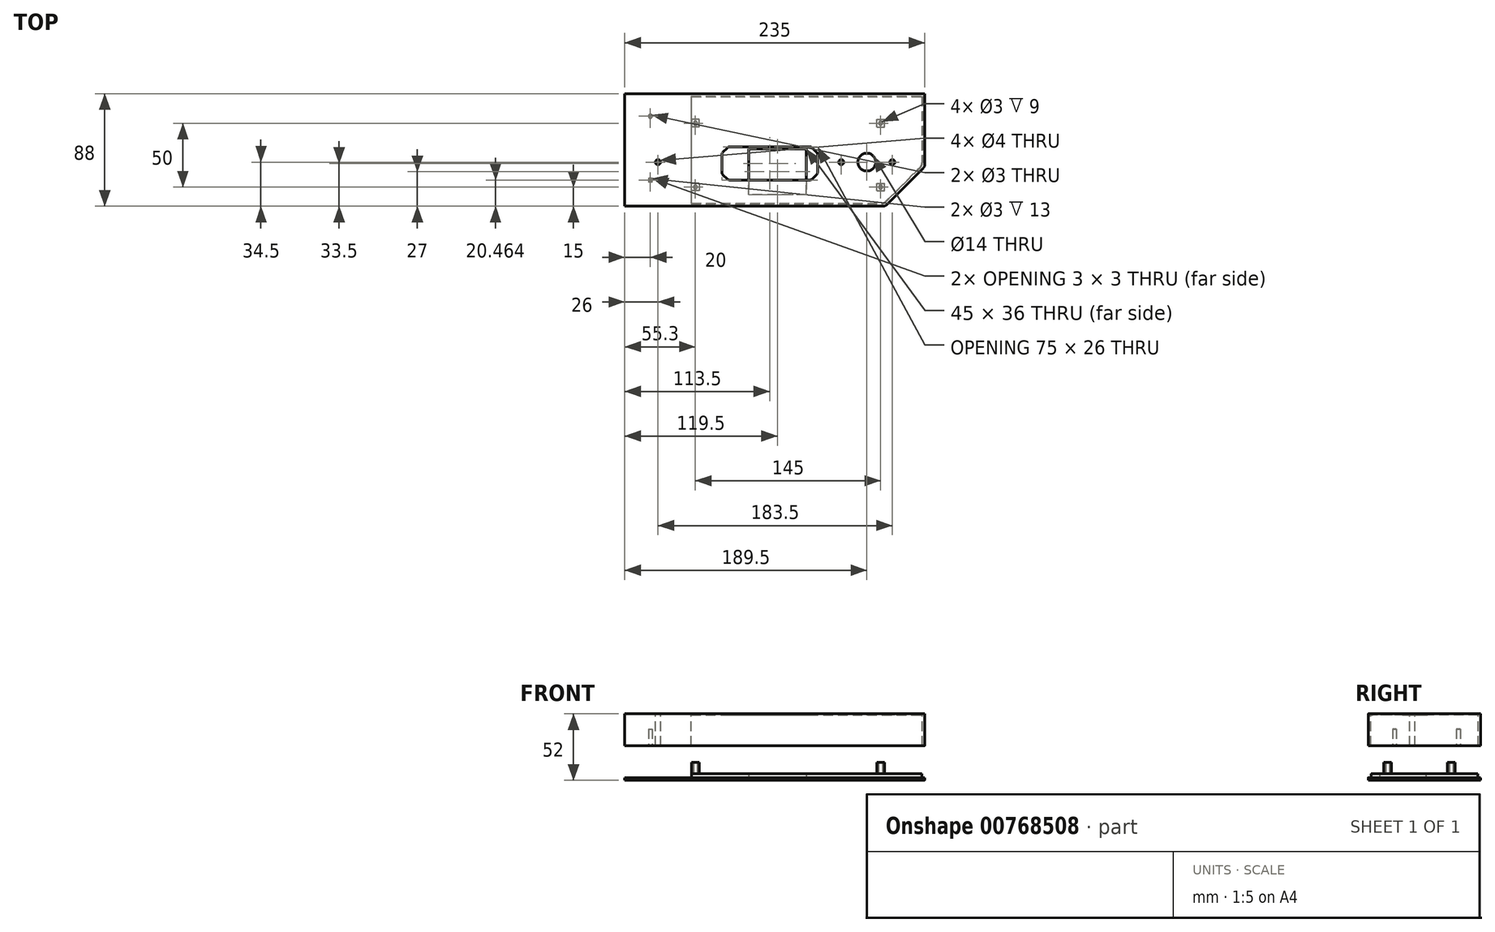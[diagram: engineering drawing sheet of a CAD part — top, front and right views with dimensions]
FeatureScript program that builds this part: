
annotation { "Feature Type Name" : "Feature", "Feature Type Description" : "" }
export const myFeature = defineFeature(function(context is Context, id is Id, definition is map)
    precondition{}
    {
        {
            var Q0;
            Q0=qCreatedBy(makeId("Top.planeOp"),FACE);
            var sketch = newSketch(context, id + "F0", { "sketchPlane" : qUnion([Q0])});
            skLineSegment(sketch, "E0.bottom", {"start": v(0, 0) * mm, "end": v(154, 0) * mm});
            skLineSegment(sketch, "E0.top", {"start": v(2, 68) * mm, "end": v(154, 68) * mm});
            skLineSegment(sketch, "E0.left", {"start": v(0, 0) * mm, "end": v(0, 68) * mm});
            skLineSegment(sketch, "E0.right", {"start": v(154, 2.83) * mm, "end": v(154, 68) * mm});
            skLineSegment(sketch, "E1", {"start": v(154, 0) * mm, "end": v(185, 31) * mm});
            skLineSegment(sketch, "E2.bottom", {"start": v(2, 68) * mm, "end": v(183, 68) * mm});
            skLineSegment(sketch, "E2.top", {"start": v(0, 88) * mm, "end": v(185, 88) * mm});
            skLineSegment(sketch, "E2.left", {"start": v(0, 68) * mm, "end": v(0, 88) * mm});
            skLineSegment(sketch, "E3.bottom", {"start": v(26, 20.5) * mm, "end": v(101, 20.5) * mm});
            skLineSegment(sketch, "E3.top", {"start": v(26, 46.5) * mm, "end": v(101, 46.5) * mm});
            skLineSegment(sketch, "E3.left", {"start": v(26, 20.5) * mm, "end": v(26, 46.5) * mm});
            skLineSegment(sketch, "E3.right", {"start": v(101, 20.5) * mm, "end": v(101, 46.5) * mm});
            skCircle(sketch, "E4", {"center": v(139.5, 34.5) * mm, "radius": 7 * mm});
            skLineSegment(sketch, "E5", {"start": v(2, 86) * mm, "end": v(2, 2) * mm});
            skLineSegment(sketch, "E6", {"start": v(2, 2) * mm, "end": v(153.17, 2) * mm});
            skLineSegment(sketch, "E7.trimOffspring", {"start": v(2, 86) * mm, "end": v(183, 86) * mm});
            skLineSegment(sketch, "E8", {"start": v(185, 31) * mm, "end": v(185, 88) * mm});
            skLineSegment(sketch, "E9", {"start": v(183, 86) * mm, "end": v(183, 31.83) * mm});
            skLineSegment(sketch, "E10.trimOffspring", {"start": v(183, 31.83) * mm, "end": v(153.17, 2) * mm});
            skCircle(sketch, "E11", {"center": v(119.5, 34.5) * mm, "radius": 2 * mm});
            skCircle(sketch, "E12", {"center": v(159.5, 34.5) * mm, "radius": 2 * mm});
            skCircle(sketch, "E13", {"center": v(-20, 34.5) * mm, "radius": 2 * mm});
            skSolve(sketch);
        }
        {
            var Q0;
            {var subQ1=sQuery(id+"F0.wireOp",EDGE,"E0.right");Q0=makeQuery(id+"F0.imprint","IMPRINT",FACE,{"disambiguationData":[TD([[makeQuery(id+"F0.imprint","IMPRINT",EDGE,{"derivedFrom":subQ1}),1.0]])]});}
            var Q1;
            {var subQ0=sQuery(id+"F0.wireOp",EDGE,"E0.right");Q1=makeQuery(id+"F0.imprint","IMPRINT",FACE,{"disambiguationData":[TD([[makeQuery(id+"F0.imprint","IMPRINT",EDGE,{"derivedFrom":subQ0}),-1.0]])]});}
            var Q2;
            {var subQ3=sQuery(id+"F0.wireOp",EDGE,"E7.trimOffspring");Q2=makeQuery(id+"F0.imprint","IMPRINT",FACE,{"disambiguationData":[TD([[makeQuery(id+"F0.imprint","IMPRINT",EDGE,{"derivedFrom":subQ3}),-1.0]])]});}
            extrude(context, id + "F1", {"entities" : qUnion([Q0, Q1, Q2]), "oppositeDirection" : true, "depth" : 1 * mm, "offsetDistance" : 25 * mm});
        }
        {
            var Q0;
            Q0=makeQuery(id+"F0.imprint","IMPRINT",FACE,{"disambiguationData":[TD([[makeQuery(id+"F0.imprint","IMPRINT",EDGE,{"derivedFrom":sQuery(id+"F0.wireOp",EDGE,"E0.bottom")}),1.0]])]});
            extrude(context, id + "F2", {"entities" : qUnion([Q0]), "operationType" : NewBodyOperationType.ADD, "oppositeDirection" : true, "depth" : 25 * mm, "offsetDistance" : 25 * mm});
        }
        {
            var Q0;
            Q0=makeQuery(id+"F2.opExtrude","SWEPT_EDGE",EDGE,{"disambiguationData":[OSD([sQuery(id+"F0.wireOp",EDGE,"E0.bottom"),sQuery(id+"F0.wireOp",EDGE,"E1")])]});
            var Q1;
            Q1=makeQuery(id+"F2.opExtrude","SWEPT_EDGE",EDGE,{"disambiguationData":[OSD([sQuery(id+"F0.wireOp",EDGE,"E1"),sQuery(id+"F0.wireOp",EDGE,"E8")])]});
            var Q2;
            Q2=makeQuery(id+"F2.opExtrude","SWEPT_EDGE",EDGE,{"disambiguationData":[OSD([sQuery(id+"F0.wireOp",EDGE,"E6"),sQuery(id+"F0.wireOp",EDGE,"E10.trimOffspring")])]});
            var Q3;
            Q3=makeQuery(id+"F2.opExtrude","SWEPT_EDGE",EDGE,{"disambiguationData":[OSD([sQuery(id+"F0.wireOp",EDGE,"E9"),sQuery(id+"F0.wireOp",EDGE,"E10.trimOffspring")])]});
            fillet(context, id + "F3", {"entities" : qUnion([Q0, Q1, Q2, Q3]), "radius" : 5 * mm, "tangentPropagation" : true, "allowEdgeOverflow" : false});
        }
        {
            var Q0;
            Q0=makeQuery(id+"F1.opExtrude","SWEPT_EDGE",EDGE,{"disambiguationData":[OSD([sQuery(id+"F0.wireOp",EDGE,"E3.top"),sQuery(id+"F0.wireOp",EDGE,"E3.left")])]});
            var Q1;
            Q1=makeQuery(id+"F1.opExtrude","SWEPT_EDGE",EDGE,{"disambiguationData":[OSD([sQuery(id+"F0.wireOp",EDGE,"E3.bottom"),sQuery(id+"F0.wireOp",EDGE,"E3.left")])]});
            var Q2;
            Q2=makeQuery(id+"F1.opExtrude","SWEPT_EDGE",EDGE,{"disambiguationData":[OSD([sQuery(id+"F0.wireOp",EDGE,"E3.bottom"),sQuery(id+"F0.wireOp",EDGE,"E3.right")])]});
            var Q3;
            Q3=makeQuery(id+"F1.opExtrude","SWEPT_EDGE",EDGE,{"disambiguationData":[OSD([sQuery(id+"F0.wireOp",EDGE,"E3.top"),sQuery(id+"F0.wireOp",EDGE,"E3.right")])]});
            chamfer(context, id + "F4", {"entities" : qUnion([Q0, Q1, Q2, Q3]), "width" : 5 * mm, "tangentPropagation" : true});
        }
        {
            var Q0;
            {var subQ0=sQuery(id+"F0.wireOp",EDGE,"E3.left");Q0=makeQuery(id+"F4.opChamfer","BLEND_EDGE",EDGE,{"blendedFrom":[makeQuery(id+"F1.opExtrude","SWEPT_EDGE",EDGE,{"disambiguationData":[OSD([sQuery(id+"F0.wireOp",EDGE,"E3.top"),subQ0])]}),makeQuery(id+"F1.opExtrude","SWEPT_FACE",FACE,{"disambiguationData":[OSD([subQ0])]})],"blendedInto":[makeQuery(id+"F1.opExtrude","SWEPT_FACE",FACE,{"disambiguationData":[OSD([subQ0])]})]});}
            var Q1;
            {var subQ0=sQuery(id+"F0.wireOp",EDGE,"E3.top");Q1=makeQuery(id+"F4.opChamfer","BLEND_EDGE",EDGE,{"blendedFrom":[makeQuery(id+"F1.opExtrude","SWEPT_EDGE",EDGE,{"disambiguationData":[OSD([subQ0,sQuery(id+"F0.wireOp",EDGE,"E3.left")])]}),makeQuery(id+"F1.opExtrude","SWEPT_FACE",FACE,{"disambiguationData":[OSD([subQ0])]})],"blendedInto":[makeQuery(id+"F1.opExtrude","SWEPT_FACE",FACE,{"disambiguationData":[OSD([subQ0])]})]});}
            var Q2;
            {var subQ0=sQuery(id+"F0.wireOp",EDGE,"E3.left");Q2=makeQuery(id+"F4.opChamfer","BLEND_EDGE",EDGE,{"blendedFrom":[makeQuery(id+"F1.opExtrude","SWEPT_EDGE",EDGE,{"disambiguationData":[OSD([sQuery(id+"F0.wireOp",EDGE,"E3.bottom"),subQ0])]}),makeQuery(id+"F1.opExtrude","SWEPT_FACE",FACE,{"disambiguationData":[OSD([subQ0])]})],"blendedInto":[makeQuery(id+"F1.opExtrude","SWEPT_FACE",FACE,{"disambiguationData":[OSD([subQ0])]})]});}
            var Q3;
            {var subQ0=sQuery(id+"F0.wireOp",EDGE,"E3.bottom");Q3=makeQuery(id+"F4.opChamfer","BLEND_EDGE",EDGE,{"blendedFrom":[makeQuery(id+"F1.opExtrude","SWEPT_EDGE",EDGE,{"disambiguationData":[OSD([subQ0,sQuery(id+"F0.wireOp",EDGE,"E3.left")])]}),makeQuery(id+"F1.opExtrude","SWEPT_FACE",FACE,{"disambiguationData":[OSD([subQ0])]})],"blendedInto":[makeQuery(id+"F1.opExtrude","SWEPT_FACE",FACE,{"disambiguationData":[OSD([subQ0])]})]});}
            var Q4;
            {var subQ0=sQuery(id+"F0.wireOp",EDGE,"E3.top");Q4=makeQuery(id+"F4.opChamfer","BLEND_EDGE",EDGE,{"blendedFrom":[makeQuery(id+"F1.opExtrude","SWEPT_EDGE",EDGE,{"disambiguationData":[OSD([subQ0,sQuery(id+"F0.wireOp",EDGE,"E3.right")])]}),makeQuery(id+"F1.opExtrude","SWEPT_FACE",FACE,{"disambiguationData":[OSD([subQ0])]})],"blendedInto":[makeQuery(id+"F1.opExtrude","SWEPT_FACE",FACE,{"disambiguationData":[OSD([subQ0])]})]});}
            var Q5;
            {var subQ0=sQuery(id+"F0.wireOp",EDGE,"E3.right");Q5=makeQuery(id+"F4.opChamfer","BLEND_EDGE",EDGE,{"blendedFrom":[makeQuery(id+"F1.opExtrude","SWEPT_EDGE",EDGE,{"disambiguationData":[OSD([sQuery(id+"F0.wireOp",EDGE,"E3.top"),subQ0])]}),makeQuery(id+"F1.opExtrude","SWEPT_FACE",FACE,{"disambiguationData":[OSD([subQ0])]})],"blendedInto":[makeQuery(id+"F1.opExtrude","SWEPT_FACE",FACE,{"disambiguationData":[OSD([subQ0])]})]});}
            var Q6;
            {var subQ0=sQuery(id+"F0.wireOp",EDGE,"E3.right");Q6=makeQuery(id+"F4.opChamfer","BLEND_EDGE",EDGE,{"blendedFrom":[makeQuery(id+"F1.opExtrude","SWEPT_EDGE",EDGE,{"disambiguationData":[OSD([sQuery(id+"F0.wireOp",EDGE,"E3.bottom"),subQ0])]}),makeQuery(id+"F1.opExtrude","SWEPT_FACE",FACE,{"disambiguationData":[OSD([subQ0])]})],"blendedInto":[makeQuery(id+"F1.opExtrude","SWEPT_FACE",FACE,{"disambiguationData":[OSD([subQ0])]})]});}
            var Q7;
            {var subQ0=sQuery(id+"F0.wireOp",EDGE,"E3.bottom");Q7=makeQuery(id+"F4.opChamfer","BLEND_EDGE",EDGE,{"blendedFrom":[makeQuery(id+"F1.opExtrude","SWEPT_EDGE",EDGE,{"disambiguationData":[OSD([subQ0,sQuery(id+"F0.wireOp",EDGE,"E3.right")])]}),makeQuery(id+"F1.opExtrude","SWEPT_FACE",FACE,{"disambiguationData":[OSD([subQ0])]})],"blendedInto":[makeQuery(id+"F1.opExtrude","SWEPT_FACE",FACE,{"disambiguationData":[OSD([subQ0])]})]});}
            fillet(context, id + "F5", {"entities" : qUnion([Q0, Q1, Q2, Q3, Q4, Q5, Q6, Q7]), "radius" : 3 * mm, "tangentPropagation" : true, "allowEdgeOverflow" : false});
        }
        {
            var Q0;
            Q0=qCreatedBy(makeId("Top.planeOp"),FACE);
            var sketch = newSketch(context, id + "F6", { "sketchPlane" : qUnion([Q0])});
            skLineSegment(sketch, "E14.bottom", {"start": v(0, 0) * mm, "end": v(-50, 0) * mm});
            skLineSegment(sketch, "E14.top", {"start": v(0, 88) * mm, "end": v(-50, 88) * mm});
            skLineSegment(sketch, "E14.left", {"start": v(0, 0) * mm, "end": v(0, 88) * mm});
            skLineSegment(sketch, "E14.right", {"start": v(-50, 0) * mm, "end": v(-50, 88) * mm});
            skSolve(sketch);
        }
        {
            var Q0;
            Q0=makeQuery(id+"F6.imprint","IMPRINT",FACE,{"disambiguationData":[TD([[makeQuery(id+"F6.imprint","IMPRINT",EDGE,{"derivedFrom":sQuery(id+"F6.wireOp",EDGE,"E14.bottom")}),-1.0]])]});
            extrude(context, id + "F7", {"entities" : qUnion([Q0]), "operationType" : NewBodyOperationType.ADD, "oppositeDirection" : true, "depth" : 25 * mm, "offsetDistance" : 25 * mm});
        }
        {
            var Q0;
            Q0=qCreatedBy(makeId("Top.planeOp"),FACE);
            cPlane(context, id + "F8", {"entities" : qUnion([Q0]), "cplaneType" : CPlaneType.OFFSET, "offset" : 50 * mm, "oppositeDirection" : true, "width" : 150 * mm, "height" : 150 * mm});
        }
        {
            var Q0;
            Q0=qCreatedBy(id+"F8.planeOp",FACE);
            var sketch = newSketch(context, id + "F9", { "sketchPlane" : qUnion([Q0])});
            skLineSegment(sketch, "E15.bottom", {"start": v(0, 0) * mm, "end": v(154, 0) * mm});
            skLineSegment(sketch, "E15.top", {"start": v(0, 88) * mm, "end": v(185, 88) * mm});
            skLineSegment(sketch, "E15.left", {"start": v(0, 0) * mm, "end": v(0, 88) * mm});
            skLineSegment(sketch, "E16", {"start": v(154, 0) * mm, "end": v(185, 31) * mm});
            skLineSegment(sketch, "E17", {"start": v(2.3, 2.3) * mm, "end": v(153.05, 2.3) * mm});
            skLineSegment(sketch, "E18", {"start": v(2.3, 85.7) * mm, "end": v(182.7, 85.7) * mm});
            skLineSegment(sketch, "E19", {"start": v(153.05, 2.3) * mm, "end": v(182.7, 31.95) * mm});
            skPoint(sketch, "E20.orphan", {"position": v(150.75, 0) * mm});
            skLineSegment(sketch, "E21.trimOffspring", {"start": v(2.3, 2.3) * mm, "end": v(2.3, 85.9) * mm});
            skLineSegment(sketch, "E22", {"start": v(185, 31) * mm, "end": v(185, 88) * mm});
            skLineSegment(sketch, "E23.trimOffspring", {"start": v(182.7, 85.7) * mm, "end": v(182.7, 31.95) * mm});
            skSolve(sketch);
        }
        {
            var Q0;
            {var subQ0=sQuery(id+"F9.wireOp",EDGE,"E17");Q0=makeQuery(id+"F9.imprint","IMPRINT",FACE,{"disambiguationData":[TD([[makeQuery(id+"F9.imprint","IMPRINT",EDGE,{"derivedFrom":subQ0}),1.0]])]});}
            extrude(context, id + "F10", {"entities" : qUnion([Q0]), "depth" : 3 * mm, "offsetDistance" : 25 * mm});
        }
        {
            var Q0;
            Q0 = qSketchRegion(id + "F9", true);
            var Q1;
            Q1=makeQuery(id+"F10.opExtrude","CAP_FACE",FACE,{"disambiguationData":[OSD([sQuery(id+"F9.wireOp",EDGE,"E17"),sQuery(id+"F9.wireOp",EDGE,"E18"),sQuery(id+"F9.wireOp",EDGE,"E19"),sQuery(id+"F9.wireOp",EDGE,"E21.trimOffspring")])],"isStart":true});
            extrude(context, id + "F11", {"entities" : qUnion([Q0, Q1]), "operationType" : NewBodyOperationType.ADD, "oppositeDirection" : true, "depth" : 2 * mm, "offsetDistance" : 25 * mm});
        }
        {
            var Q0;
            Q0=makeQuery(id+"F11.opExtrude","SWEPT_FACE",FACE,{"disambiguationData":[OSD([sQuery(id+"F9.wireOp",EDGE,"E15.left")])]});
            extrude(context, id + "F12", {"entities" : qUnion([Q0]), "operationType" : NewBodyOperationType.ADD, "depth" : 50 * mm, "offsetDistance" : 25 * mm});
        }
        {
            var Q0;
            Q0=makeQuery(id+"F10.opExtrude","SWEPT_EDGE",EDGE,{"disambiguationData":[OSD([sQuery(id+"F9.wireOp",EDGE,"E17"),sQuery(id+"F9.wireOp",EDGE,"E19")])]});
            var Q1;
            Q1=makeQuery(id+"F11.opExtrude","SWEPT_EDGE",EDGE,{"disambiguationData":[OSD([sQuery(id+"F9.wireOp",EDGE,"E15.bottom"),sQuery(id+"F9.wireOp",EDGE,"E16")])]});
            var Q2;
            Q2=makeQuery(id+"F10.opExtrude","SWEPT_EDGE",EDGE,{"disambiguationData":[OSD([sQuery(id+"F9.wireOp",EDGE,"E19"),sQuery(id+"F9.wireOp",EDGE,"E23.trimOffspring")])]});
            var Q3;
            Q3=makeQuery(id+"F11.opExtrude","SWEPT_EDGE",EDGE,{"disambiguationData":[OSD([sQuery(id+"F9.wireOp",EDGE,"E16"),sQuery(id+"F9.wireOp",EDGE,"E22")])]});
            fillet(context, id + "F13", {"entities" : qUnion([Q0, Q1, Q2, Q3]), "radius" : 5 * mm, "tangentPropagation" : true, "allowEdgeOverflow" : false});
        }
        {
            var Q0;
            {var subQ0=sQuery(id+"F9.wireOp",EDGE,"E15.left");var subQ1=sQuery(id+"F9.wireOp",EDGE,"E21.trimOffspring");var subQ2=sQuery(id+"F9.wireOp",EDGE,"E19");var subQ3=sQuery(id+"F9.wireOp",EDGE,"E18");var subQ4=sQuery(id+"F9.wireOp",EDGE,"E17");Q0=makeQuery(id+"F12.boolean.opBoolean","MERGE",FACE,{"derivedFrom":[makeQuery(id+"F11.boolean.opBoolean","MERGE",FACE,{"derivedFrom":[makeQuery(id+"F11.opExtrude","CAP_FACE",FACE,{"disambiguationData":[OSD([sQuery(id+"F9.wireOp",EDGE,"E15.bottom"),sQuery(id+"F9.wireOp",EDGE,"E15.top"),subQ0,sQuery(id+"F9.wireOp",EDGE,"E16"),subQ4,subQ3,subQ2,subQ1])],"isStart":false}),makeQuery(id+"F11.opExtrude","CAP_FACE",FACE,{"disambiguationData":[OSD([subQ4,subQ3,subQ2,subQ1])],"isStart":false})]}),makeQuery(id+"F12.opExtrude","SWEPT_FACE",FACE,{"disambiguationData":[OSD([subQ0]),TDD([makeQuery(id+"F11.opExtrude","CAP_EDGE",EDGE,{"disambiguationData":[OSD([subQ0])],"isStart":false})])]})]});}
            var sketch = newSketch(context, id + "F14", { "sketchPlane" : qUnion([Q0])});
            skLineSegment(sketch, "E24.bottom", {"start": v(47, -34) * mm, "end": v(92, -34) * mm});
            skLineSegment(sketch, "E24.top", {"start": v(47, -45) * mm, "end": v(92, -45) * mm});
            skLineSegment(sketch, "E24.left", {"start": v(47, -34) * mm, "end": v(47, -45) * mm});
            skLineSegment(sketch, "E24.right", {"start": v(92, -34) * mm, "end": v(92, -45) * mm});
            skCircle(sketch, "E25", {"center": v(5.3, -65) * mm, "radius": 1.5 * mm});
            skCircle(sketch, "E26", {"center": v(150.3, -65) * mm, "radius": 1.5 * mm});
            skCircle(sketch, "E27", {"center": v(150.3, -15) * mm, "radius": 1.5 * mm});
            skCircle(sketch, "E28", {"center": v(5.3, -15) * mm, "radius": 1.5 * mm});
            skLineSegment(sketch, "E29.bottom", {"start": v(2.3, -68) * mm, "end": v(8.3, -68) * mm});
            skLineSegment(sketch, "E29.top", {"start": v(2.3, -62) * mm, "end": v(8.3, -62) * mm});
            skLineSegment(sketch, "E29.left", {"start": v(2.3, -68) * mm, "end": v(2.3, -62) * mm});
            skLineSegment(sketch, "E29.right", {"start": v(8.3, -68) * mm, "end": v(8.3, -62) * mm});
            skLineSegment(sketch, "E30.bottom", {"start": v(153.3, -68) * mm, "end": v(147.3, -68) * mm});
            skLineSegment(sketch, "E30.top", {"start": v(153.3, -62) * mm, "end": v(147.3, -62) * mm});
            skLineSegment(sketch, "E30.left", {"start": v(153.3, -68) * mm, "end": v(153.3, -62) * mm});
            skLineSegment(sketch, "E30.right", {"start": v(147.3, -68) * mm, "end": v(147.3, -62) * mm});
            skLineSegment(sketch, "E31.bottom", {"start": v(2.3, -12) * mm, "end": v(8.3, -12) * mm});
            skLineSegment(sketch, "E31.top", {"start": v(2.3, -18) * mm, "end": v(8.3, -18) * mm});
            skLineSegment(sketch, "E31.left", {"start": v(2.3, -12) * mm, "end": v(2.3, -18) * mm});
            skLineSegment(sketch, "E31.right", {"start": v(8.3, -12) * mm, "end": v(8.3, -18) * mm});
            skLineSegment(sketch, "E32.bottom", {"start": v(153.3, -18) * mm, "end": v(147.3, -18) * mm});
            skLineSegment(sketch, "E32.top", {"start": v(153.3, -12) * mm, "end": v(147.3, -12) * mm});
            skLineSegment(sketch, "E32.left", {"start": v(153.3, -18) * mm, "end": v(153.3, -12) * mm});
            skLineSegment(sketch, "E32.right", {"start": v(147.3, -18) * mm, "end": v(147.3, -12) * mm});
            skSolve(sketch);
        }
        {
            var Q0;
            Q0=makeQuery(id+"F14.imprint","IMPRINT",FACE,{"disambiguationData":[TD([[makeQuery(id+"F14.imprint","IMPRINT",EDGE,{"derivedFrom":sQuery(id+"F14.wireOp",EDGE,"E24.bottom")}),-1.0]])]});
            extrude(context, id + "F15", {"entities" : qUnion([Q0]), "operationType" : NewBodyOperationType.REMOVE, "oppositeDirection" : true, "depth" : 25 * mm, "offsetDistance" : 25 * mm});
        }
        {
            var Q0;
            Q0=makeQuery(id+"F14.imprint","IMPRINT",FACE,{"disambiguationData":[TD([[makeQuery(id+"F14.imprint","IMPRINT",EDGE,{"derivedFrom":sQuery(id+"F14.wireOp",EDGE,"E25")}),-1.0]])]});
            var Q1;
            Q1=makeQuery(id+"F14.imprint","IMPRINT",FACE,{"disambiguationData":[TD([[makeQuery(id+"F14.imprint","IMPRINT",EDGE,{"derivedFrom":sQuery(id+"F14.wireOp",EDGE,"E26")}),-1.0]])]});
            var Q2;
            Q2=makeQuery(id+"F14.imprint","IMPRINT",FACE,{"disambiguationData":[TD([[makeQuery(id+"F14.imprint","IMPRINT",EDGE,{"derivedFrom":sQuery(id+"F14.wireOp",EDGE,"E27")}),-1.0]])]});
            var Q3;
            Q3=makeQuery(id+"F14.imprint","IMPRINT",FACE,{"disambiguationData":[TD([[makeQuery(id+"F14.imprint","IMPRINT",EDGE,{"derivedFrom":sQuery(id+"F14.wireOp",EDGE,"E28")}),-1.0]])]});
            extrude(context, id + "F16", {"entities" : qUnion([Q0, Q1, Q2, Q3]), "operationType" : NewBodyOperationType.ADD, "oppositeDirection" : true, "depth" : (9 + 5) * mm, "offsetDistance" : 25 * mm});
        }
        {
            var Q0;
            Q0=makeQuery(id+"F14.imprint","IMPRINT",FACE,{"disambiguationData":[TD([[makeQuery(id+"F14.imprint","IMPRINT",EDGE,{"derivedFrom":sQuery(id+"F14.wireOp",EDGE,"E24.bottom")}),1.0]])]});
            var sketch = newSketch(context, id + "F17", { "sketchPlane" : qUnion([Q0])});
            skCircle(sketch, "E33", {"center": v(-30, -20.46) * mm, "radius": 1.5 * mm});
            skCircle(sketch, "E34", {"center": v(-30, -70.46) * mm, "radius": 1.5 * mm});
            skSolve(sketch);
        }
        {
            var Q0;
            Q0 = qSketchRegion(id + "F17", true);
            extrude(context, id + "F18", {"entities" : qUnion([Q0]), "operationType" : NewBodyOperationType.REMOVE, "oppositeDirection" : true, "depth" : 40 * mm, "offsetDistance" : 25 * mm});
        }
        {
            var Q0;
            Q0=makeQuery(id+"F15.boolean.opBoolean","COPY",FACE,{"derivedFrom":makeQuery(id+"F15.opExtrude","SWEPT_FACE",FACE,{"disambiguationData":[OSD([sQuery(id+"F14.wireOp",EDGE,"E24.bottom")])]})});
            extrude(context, id + "F19", {"entities" : qUnion([Q0]), "operationType" : NewBodyOperationType.REMOVE, "oppositeDirection" : true, "depth" : 25 * mm, "offsetDistance" : 25 * mm});
        }
        {
            var Q0;
            {var subQ0=sQuery(id+"F0.wireOp",EDGE,"E10.trimOffspring");var subQ1=sQuery(id+"F0.wireOp",EDGE,"E9");var subQ2=sQuery(id+"F0.wireOp",EDGE,"E7.trimOffspring");var subQ3=sQuery(id+"F0.wireOp",EDGE,"E6");var subQ4=sQuery(id+"F0.wireOp",EDGE,"E5");Q0=makeQuery(id+"F7.boolean.opBoolean","MERGE",FACE,{"derivedFrom":[makeQuery(id+"F2.boolean.opBoolean","MERGE",FACE,{"derivedFrom":[makeQuery(id+"F1.opExtrude","CAP_FACE",FACE,{"disambiguationData":[OSD([sQuery(id+"F0.wireOp",EDGE,"E3.bottom"),sQuery(id+"F0.wireOp",EDGE,"E3.top"),sQuery(id+"F0.wireOp",EDGE,"E3.left"),sQuery(id+"F0.wireOp",EDGE,"E3.right"),sQuery(id+"F0.wireOp",EDGE,"E4"),subQ4,subQ3,subQ2,subQ1,subQ0,sQuery(id+"F0.wireOp",EDGE,"E11"),sQuery(id+"F0.wireOp",EDGE,"E12")])],"isStart":true}),makeQuery(id+"F2.opExtrude","CAP_FACE",FACE,{"disambiguationData":[OSD([sQuery(id+"F0.wireOp",EDGE,"E0.bottom"),sQuery(id+"F0.wireOp",EDGE,"E0.left"),sQuery(id+"F0.wireOp",EDGE,"E1"),sQuery(id+"F0.wireOp",EDGE,"E2.top"),sQuery(id+"F0.wireOp",EDGE,"E2.left"),subQ4,subQ3,subQ2,sQuery(id+"F0.wireOp",EDGE,"E8"),subQ1,subQ0])],"isStart":true})]}),makeQuery(id+"F7.opExtrude","CAP_FACE",FACE,{"disambiguationData":[OSD([sQuery(id+"F6.wireOp",EDGE,"E14.bottom"),sQuery(id+"F6.wireOp",EDGE,"E14.top"),sQuery(id+"F6.wireOp",EDGE,"E14.left"),sQuery(id+"F6.wireOp",EDGE,"E14.right")])],"isStart":true})]});}
            var sketch = newSketch(context, id + "F20", { "sketchPlane" : qUnion([Q0])});
            skCircle(sketch, "E35", {"center": v(-24, 34.5) * mm, "radius": 2 * mm});
            skSolve(sketch);
        }
        {
            var Q0;
            Q0 = qSketchRegion(id + "F20", true);
            extrude(context, id + "F21", {"entities" : qUnion([Q0]), "operationType" : NewBodyOperationType.REMOVE, "oppositeDirection" : true, "depth" : 93.4 * mm, "offsetDistance" : 25 * mm});
        }
    });
